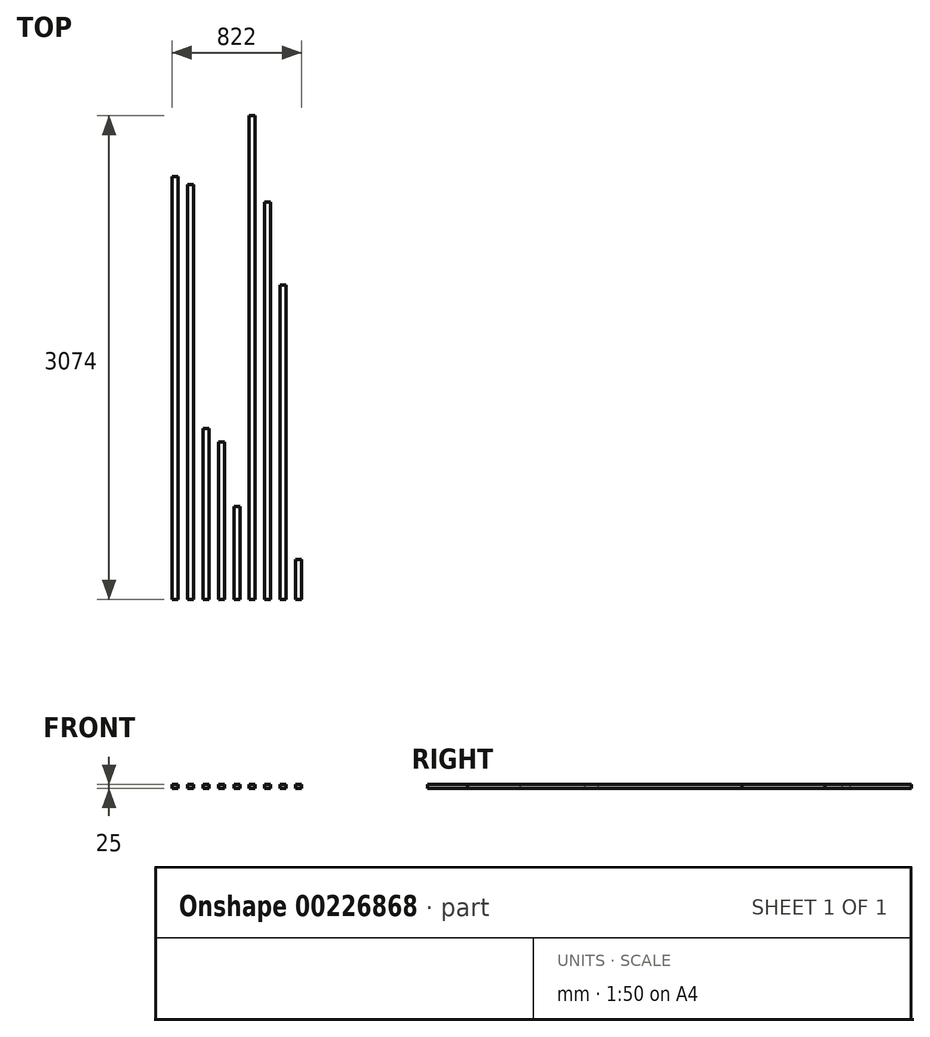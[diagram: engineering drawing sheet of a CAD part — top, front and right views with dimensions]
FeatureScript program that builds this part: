
annotation { "Feature Type Name" : "Feature", "Feature Type Description" : "" }
export const myFeature = defineFeature(function(context is Context, id is Id, definition is map)
    precondition{}
    {
        {
            var Q0;
            Q0=qCreatedBy(makeId("Front.planeOp"),FACE);
            var sketch = newSketch(context, id + "F0", { "sketchPlane" : qUnion([Q0])});
            skLineSegment(sketch, "E0.bottom", {"start": v(0, 0) * mm, "end": v(38, 0) * mm});
            skLineSegment(sketch, "E0.top", {"start": v(0, 25) * mm, "end": v(38, 25) * mm});
            skLineSegment(sketch, "E0.left", {"start": v(0, 0) * mm, "end": v(0, 25) * mm});
            skLineSegment(sketch, "E0.right", {"start": v(38, 0) * mm, "end": v(38, 25) * mm});
            skLineSegment(sketch, "E1.bottom", {"start": v(98, 0) * mm, "end": v(136, 0) * mm});
            skLineSegment(sketch, "E1.top", {"start": v(98, 25) * mm, "end": v(136, 25) * mm});
            skLineSegment(sketch, "E1.left", {"start": v(98, 0) * mm, "end": v(98, 25) * mm});
            skLineSegment(sketch, "E1.right", {"start": v(136, 0) * mm, "end": v(136, 25) * mm});
            skLineSegment(sketch, "E2.bottom", {"start": v(196, 0) * mm, "end": v(234, 0) * mm});
            skLineSegment(sketch, "E2.top", {"start": v(196, 25) * mm, "end": v(234, 25) * mm});
            skLineSegment(sketch, "E2.left", {"start": v(196, 0) * mm, "end": v(196, 25) * mm});
            skLineSegment(sketch, "E2.right", {"start": v(234, 0) * mm, "end": v(234, 25) * mm});
            skLineSegment(sketch, "E3.bottom", {"start": v(294, 0) * mm, "end": v(332, 0) * mm});
            skLineSegment(sketch, "E3.top", {"start": v(294, 25) * mm, "end": v(332, 25) * mm});
            skLineSegment(sketch, "E3.left", {"start": v(294, 0) * mm, "end": v(294, 25) * mm});
            skLineSegment(sketch, "E3.right", {"start": v(332, 0) * mm, "end": v(332, 25) * mm});
            skLineSegment(sketch, "E4.bottom", {"start": v(392, 0) * mm, "end": v(430, 0) * mm});
            skLineSegment(sketch, "E4.top", {"start": v(392, 25) * mm, "end": v(430, 25) * mm});
            skLineSegment(sketch, "E4.left", {"start": v(392, 0) * mm, "end": v(392, 25) * mm});
            skLineSegment(sketch, "E4.right", {"start": v(430, 0) * mm, "end": v(430, 25) * mm});
            skLineSegment(sketch, "E5.bottom", {"start": v(490, 0) * mm, "end": v(528, 0) * mm});
            skLineSegment(sketch, "E5.top", {"start": v(490, 25) * mm, "end": v(528, 25) * mm});
            skLineSegment(sketch, "E5.left", {"start": v(490, 0) * mm, "end": v(490, 25) * mm});
            skLineSegment(sketch, "E5.right", {"start": v(528, 0) * mm, "end": v(528, 25) * mm});
            skPoint(sketch, "E6.oppositeSnap0", {"position": v(19, 25) * mm});
            skLineSegment(sketch, "E6.bottom", {"start": v(588, 0) * mm, "end": v(626, 0) * mm});
            skLineSegment(sketch, "E6.top", {"start": v(588, 25) * mm, "end": v(626, 25) * mm});
            skLineSegment(sketch, "E6.left", {"start": v(588, 0) * mm, "end": v(588, 25) * mm});
            skLineSegment(sketch, "E6.right", {"start": v(626, 0) * mm, "end": v(626, 25) * mm});
            skLineSegment(sketch, "E7.bottom", {"start": v(686, 0) * mm, "end": v(724, 0) * mm});
            skLineSegment(sketch, "E7.top", {"start": v(686, 25) * mm, "end": v(724, 25) * mm});
            skLineSegment(sketch, "E7.left", {"start": v(686, 0) * mm, "end": v(686, 25) * mm});
            skLineSegment(sketch, "E7.right", {"start": v(724, 0) * mm, "end": v(724, 25) * mm});
            skLineSegment(sketch, "E8.bottom", {"start": v(784, 0) * mm, "end": v(822, 0) * mm});
            skLineSegment(sketch, "E8.top", {"start": v(784, 25) * mm, "end": v(822, 25) * mm});
            skLineSegment(sketch, "E8.left", {"start": v(784, 0) * mm, "end": v(784, 25) * mm});
            skLineSegment(sketch, "E8.right", {"start": v(822, 0) * mm, "end": v(822, 25) * mm});
            skSolve(sketch);
        }
        {
            var Q0;
            Q0=makeQuery(id+"F0.imprint","IMPRINT",FACE,{"disambiguationData":[TD([[makeQuery(id+"F0.imprint","IMPRINT",EDGE,{"derivedFrom":sQuery(id+"F0.wireOp",EDGE,"E0.bottom")}),1.0]])]});
            extrude(context, id + "F1", {"entities" : qUnion([Q0]), "oppositeDirection" : true, "depth" : 2685 * mm});
        }
        {
            var Q0;
            Q0=makeQuery(id+"F0.imprint","IMPRINT",FACE,{"disambiguationData":[TD([[makeQuery(id+"F0.imprint","IMPRINT",EDGE,{"derivedFrom":sQuery(id+"F0.wireOp",EDGE,"E1.bottom")}),1.0]])]});
            extrude(context, id + "F2", {"entities" : qUnion([Q0]), "oppositeDirection" : true, "depth" : 2635 * mm});
        }
        {
            var Q0;
            Q0=makeQuery(id+"F0.imprint","IMPRINT",FACE,{"disambiguationData":[TD([[makeQuery(id+"F0.imprint","IMPRINT",EDGE,{"derivedFrom":sQuery(id+"F0.wireOp",EDGE,"E2.bottom")}),1.0]])]});
            extrude(context, id + "F3", {"entities" : qUnion([Q0]), "oppositeDirection" : true, "depth" : 1085 * mm});
        }
        {
            var Q0;
            Q0=makeQuery(id+"F0.imprint","IMPRINT",FACE,{"disambiguationData":[TD([[makeQuery(id+"F0.imprint","IMPRINT",EDGE,{"derivedFrom":sQuery(id+"F0.wireOp",EDGE,"E3.bottom")}),1.0]])]});
            extrude(context, id + "F4", {"entities" : qUnion([Q0]), "oppositeDirection" : true, "depth" : 1000 * mm});
        }
        {
            var Q0;
            Q0=makeQuery(id+"F0.imprint","IMPRINT",FACE,{"disambiguationData":[TD([[makeQuery(id+"F0.imprint","IMPRINT",EDGE,{"derivedFrom":sQuery(id+"F0.wireOp",EDGE,"E4.bottom")}),1.0]])]});
            extrude(context, id + "F5", {"entities" : qUnion([Q0]), "oppositeDirection" : true, "depth" : 590 * mm});
        }
        {
            var Q0;
            Q0=makeQuery(id+"F0.imprint","IMPRINT",FACE,{"disambiguationData":[TD([[makeQuery(id+"F0.imprint","IMPRINT",EDGE,{"derivedFrom":sQuery(id+"F0.wireOp",EDGE,"E5.bottom")}),1.0]])]});
            extrude(context, id + "F6", {"entities" : qUnion([Q0]), "oppositeDirection" : true, "depth" : 3074 * mm});
        }
        {
            var Q0;
            Q0=makeQuery(id+"F0.imprint","IMPRINT",FACE,{"disambiguationData":[TD([[makeQuery(id+"F0.imprint","IMPRINT",EDGE,{"derivedFrom":sQuery(id+"F0.wireOp",EDGE,"E6.bottom")}),1.0]])]});
            extrude(context, id + "F7", {"entities" : qUnion([Q0]), "oppositeDirection" : true, "depth" : 2524 * mm});
        }
        {
            var Q0;
            Q0=makeQuery(id+"F0.imprint","IMPRINT",FACE,{"disambiguationData":[TD([[makeQuery(id+"F0.imprint","IMPRINT",EDGE,{"derivedFrom":sQuery(id+"F0.wireOp",EDGE,"E7.bottom")}),1.0]])]});
            extrude(context, id + "F8", {"entities" : qUnion([Q0]), "oppositeDirection" : true, "depth" : 1996 * mm});
        }
        {
            var Q0;
            Q0=makeQuery(id+"F0.imprint","IMPRINT",FACE,{"disambiguationData":[TD([[makeQuery(id+"F0.imprint","IMPRINT",EDGE,{"derivedFrom":sQuery(id+"F0.wireOp",EDGE,"E8.bottom")}),1.0]])]});
            extrude(context, id + "F9", {"entities" : qUnion([Q0]), "oppositeDirection" : true, "depth" : 253 * mm});
        }
    });
